# Revit family: Basin-Wall-Caroma Luna Hand
name_source: partatom
category: Plumbing Fixtures
revit_build: Autodesk Revit 2015 (Build: 20160512_0715(x64)
units: mm (PartAtom-declared; Revit-internal decimal feet)

## types (2) — shared parameters
3 Tapholes = No
Assembly Code = D2010310
CW Connection = No
Capacity_ANZRS = 0.0 L
Default Elevation = 865 mm  [stored 2.83793 ft]
Description = Caroma Luna Hand Wall Basin
HW Connection = No
Height_ANZRS = 158 mm
Length_ANZRS = 450 mm  [stored 1.47638 ft]
Manufacturer = GWA Bathrooms & Kitchens
Material_ANZRS = Porcelain-White-Caroma
ModifiedIssue_ANZRS = 20170216 $
Tap Penetrations = 100 mm  [stored 0.328084 ft]
Type Comments = White Only, Overflow Only, Chrome flush fitting waste and white plug supplied
URL = http://specify.caroma.com.au
Vent Connection = No
WFU = 1
Waste = Metal-Chrome-Caroma
Waste Connection = Yes
Width_ANZRS = 250 mm  [stored 0.82021 ft]
zero-valued in all types: WasteOutlet_ANZRS

## per-type parameters (varying)
| type | 1 Taphole | Model | Spout Penetration |
| Luna - 0 Tap Holes | No | 873705W | 100 mm  [stored 0.328084 ft] |
| Luna - 1 Tap Hole | Yes | 873715W | 0 mm  [stored 0 ft] |

note: [stored X ft] marks values corroborated as IEEE doubles in the binary element streams (Revit-internal decimal feet)

## geometry (parser evidence)
native form markers: Blend x12, Sweep x2
no freeform markers — native parametric forms only
